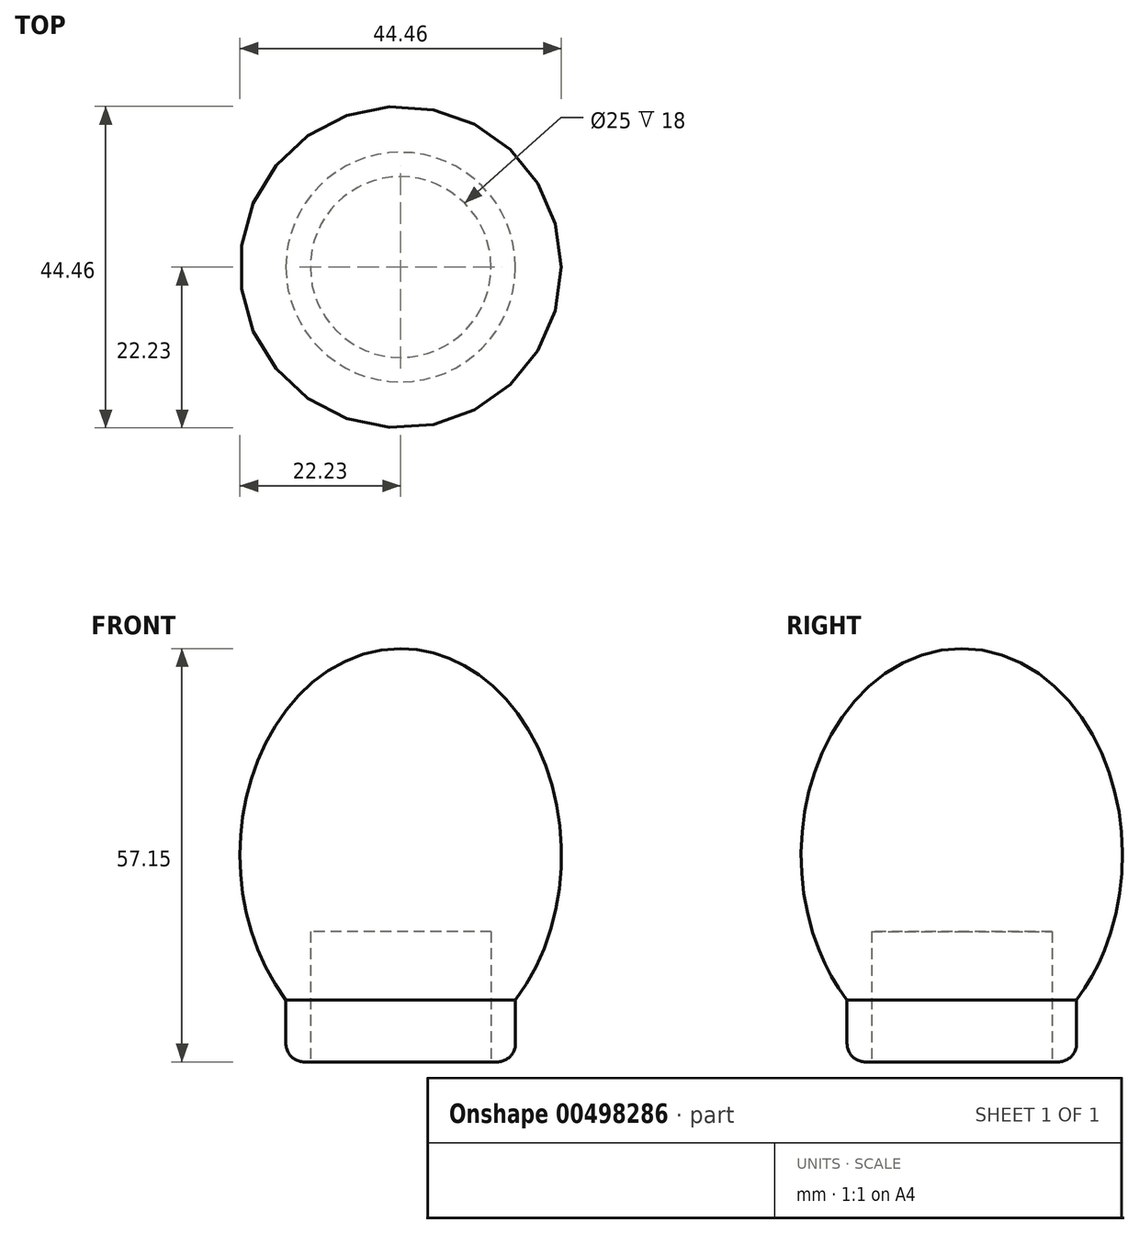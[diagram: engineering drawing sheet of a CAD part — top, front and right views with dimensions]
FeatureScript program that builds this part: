
annotation { "Feature Type Name" : "Feature", "Feature Type Description" : "" }
export const myFeature = defineFeature(function(context is Context, id is Id, definition is map)
    precondition{}
    {
        {
            var Q0;
            Q0=qCreatedBy(makeId("Front.planeOp"),FACE);
            var sketch = newSketch(context, id + "F0", { "sketchPlane" : qUnion([Q0])});
            skLineSegment(sketch, "E0", {"start": v(0, 0) * mm, "end": v(0, 57.15) * mm});
            skEllipticalArc(sketch, "E1", {});
            const initialGuessF0  = {"E1": [0, 0.028575, 0, -1, 0.028575, 0.022225, 0, 3.141592653589793]};
            skSetInitialGuess(sketch, initialGuessF0);
            skSolve(sketch);
        }
        {
            var Q0;
            Q0 = qSketchRegion(id + "F0", true);
            var Q1;
            Q1=sQuery(id+"F0.wireOp",EDGE,"E0");
            revolve(context, id + "F1", {"entities" : qUnion([Q0]), "axis" : qUnion([Q1]), "revolveType" : RevolveType.FULL});
        }
        {
            var Q0;
            Q0=qCreatedBy(makeId("Top.planeOp"),FACE);
            var sketch = newSketch(context, id + "F2", { "sketchPlane" : qUnion([Q0])});
            skCircle(sketch, "E2", {"center": v(0, 0) * mm, "radius": 15.88 * mm});
            skSolve(sketch);
        }
        {
            var Q0;
            Q0 = qSketchRegion(id + "F2", true);
            extrude(context, id + "F3", {"entities" : qUnion([Q0]), "operationType" : NewBodyOperationType.ADD, "depth" : 28.57 * mm});
        }
        {
            var Q0;
            Q0=qCreatedBy(makeId("Top.planeOp"),FACE);
            var sketch = newSketch(context, id + "F4", { "sketchPlane" : qUnion([Q0])});
            skCircle(sketch, "E3", {"center": v(0, 0) * mm, "radius": 12.5 * mm});
            skSolve(sketch);
        }
        {
            var Q0;
            Q0 = qSketchRegion(id + "F4", true);
            extrude(context, id + "F5", {"entities" : qUnion([Q0]), "operationType" : NewBodyOperationType.REMOVE, "depth" : 18 * mm});
        }
        {
            var Q0;
            Q0=makeQuery(id+"F3.opExtrude","CAP_EDGE",EDGE,{"disambiguationData":[OSD([sQuery(id+"F2.wireOp",EDGE,"E2")])],"isStart":true});
            fillet(context, id + "F6", {"entities" : qUnion([Q0]), "radius" : 2.54 * mm, "tangentPropagation" : true, "allowEdgeOverflow" : false});
        }
    });
